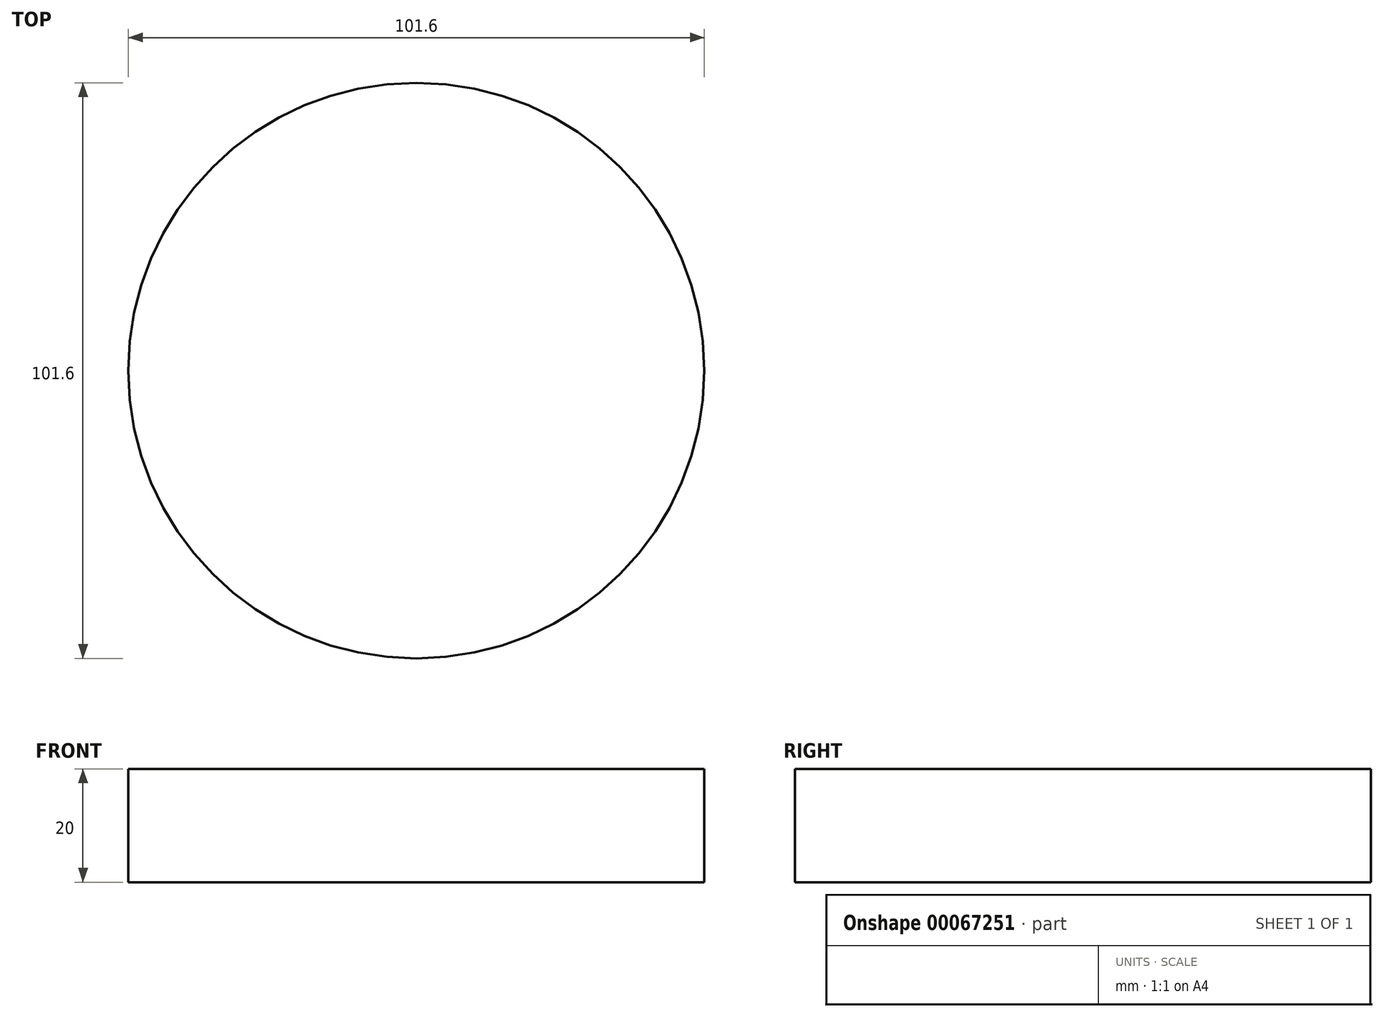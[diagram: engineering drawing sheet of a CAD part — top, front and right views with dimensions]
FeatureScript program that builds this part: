
annotation { "Feature Type Name" : "Feature", "Feature Type Description" : "" }
export const myFeature = defineFeature(function(context is Context, id is Id, definition is map)
    precondition{}
    {
        {
            var Q0;
            Q0=qCreatedBy(makeId("Top.planeOp"),FACE);
            var sketch = newSketch(context, id + "F0", { "sketchPlane" : qUnion([Q0])});
            skCircle(sketch, "E0", {"center": v(0, 0) * mm, "radius": 50.8 * mm});
            skSolve(sketch);
        }
        {
            var Q0;
            Q0=qSketchRegion(id+"F0",true);
            extrude(context, id + "F1", {"entities" : qUnion([Q0]), "depth" : 20 * mm});
        }
    });
